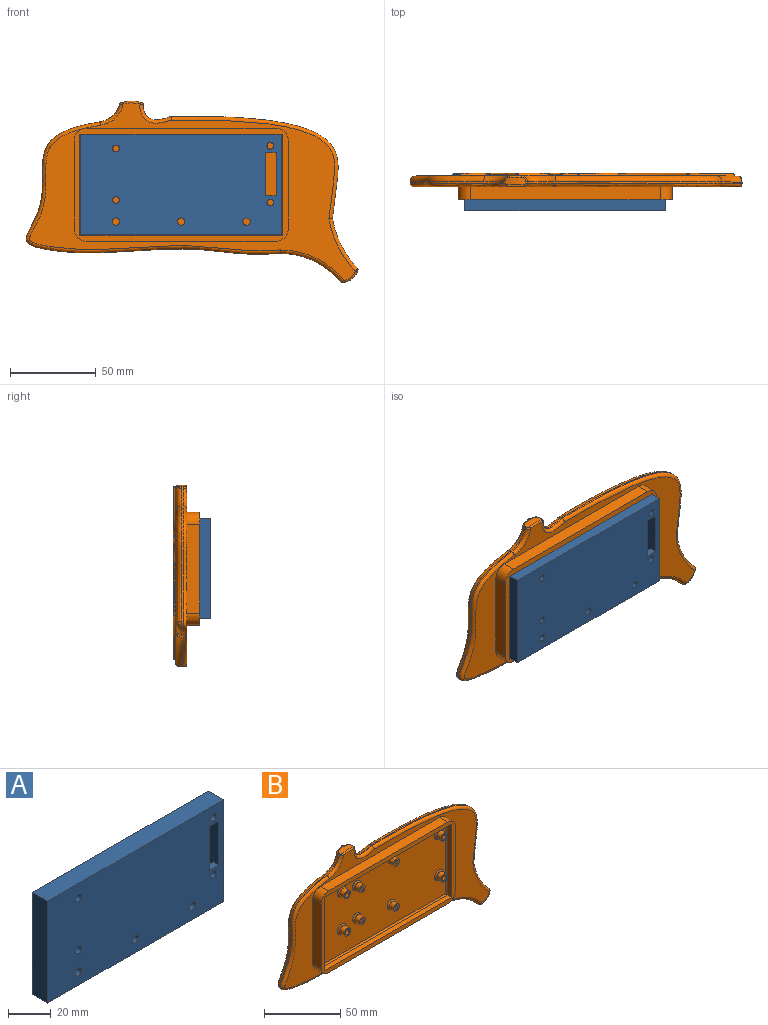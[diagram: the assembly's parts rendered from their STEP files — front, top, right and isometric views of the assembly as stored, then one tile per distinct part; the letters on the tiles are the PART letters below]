
ASSEMBLY  parts=2 mates=1
PART A: 21 faces, bbox 117x10.2x58.6 mm
  f0: cylinder r=2mm len=4mm, axis (0,-1,0), area 47.9mm2, adj f7,f8
  f1: cylinder r=2mm len=4mm, axis (0,-1,0), area 47.9mm2, adj f7,f8
  f2: cylinder r=2mm len=4mm, axis (0,-1,0), area 47.9mm2, adj f7,f8
  f3: cylinder r=2mm len=4mm, axis (0,-1,0), area 47.9mm2, adj f7,f8
  f4: cylinder r=2.12mm len=10.16mm, axis (0,-1,0), area 135.7mm2, adj f8,f17
  f5: cylinder r=2.12mm len=10.16mm, axis (0,-1,0), area 135.7mm2, adj f8,f17
  f6: cylinder r=2.12mm len=10.16mm, axis (0,-1,0), area 135.7mm2, adj f8,f17
  f7: plane 110.53x42.74mm, normal (0,1,0), area 4512.5mm2, adj f0,f1,f2,f3,f13,f14,f15,f16
  f8: plane 117x58.61mm, normal (0,-1,0), area 6603.3mm2, adj f0,f1,f2,f3,f4,f5,f6,f9
  f9: plane 58.61x10.16mm, normal (1,0,0), area 595.5mm2, adj f8,f10,f12,f17
  f10: plane 117x10.16mm, normal (0,0,-1), area 1188.7mm2, adj f8,f9,f11,f17
  f11: plane 58.61x10.16mm, normal (-1,0,0), area 595.5mm2, adj f8,f10,f12,f17
  f12: plane 117x10.16mm, normal (0,0,1), area 1188.7mm2, adj f8,f9,f11,f17
  f13: plane 42.74x10.16mm, normal (-1,0,0), area 368.2mm2, adj f7,f8,f14,f16,f17,f18,f20
  f14: plane 6.35x3.81mm, normal (0,0,1), area 24.2mm2, adj f7,f8,f13,f15
  f15: plane 25.4x3.81mm, normal (1,0,0), area 96.8mm2, adj f7,f8,f14,f16
  f16: plane 6.35x3.81mm, normal (0,0,-1), area 24.2mm2, adj f7,f8,f13,f15
  f17: plane 117x58.61mm, normal (0,1,0), area 2090.8mm2, adj f4,f5,f6,f9,f10,f11,f12,f13
  f18: plane 110.53x6.35mm, normal (0,0,1), area 701.9mm2, adj f7,f13,f17,f19
  f19: plane 42.74x6.35mm, normal (1,0,0), area 271.4mm2, adj f7,f17,f18,f20
  f20: plane 110.53x6.35mm, normal (0,0,-1), area 701.9mm2, adj f7,f13,f17,f19
PART B: 153 faces, bbox 196.2x17.7x108.7 mm
  f0: cylinder r=1mm len=0.93mm, axis (0,-1,0), area 0.9mm2, adj f56,f57,f121,f123
  f1: torus R=4mm, axis (0,-1,0), area 33.2mm2, adj f22,f34
  f2: torus R=3.75mm, axis (0,-1,0), area 30.7mm2, adj f16,f34
  f3: torus R=3.75mm, axis (0,-1,0), area 30.7mm2, adj f18,f34
  f4: torus R=4mm, axis (0,-1,0), area 33.2mm2, adj f20,f34
  f5: torus R=3.75mm, axis (0,-1,0), area 30.7mm2, adj f12,f34
  f6: torus R=4mm, axis (0,-1,0), area 33.2mm2, adj f8,f34
  f7: torus R=4mm, axis (0,-1,0), area 33.2mm2, adj f10,f34
  f8: cylinder r=3mm len=6mm, axis (0,-1,0), area 76.9mm2, adj f6,f49
  f9: cylinder r=1.88mm len=5.08mm, axis (0,-1,0), area 59.8mm2, adj f49,f50
  f10: cylinder r=3mm len=6mm, axis (0,-1,0), area 76.9mm2, adj f7,f47
  f11: cylinder r=1.88mm len=5.08mm, axis (0,-1,0), area 59.8mm2, adj f47,f48
  f12: cylinder r=2.75mm len=5.5mm, axis (0,-1,0), area 70.5mm2, adj f5,f45
  f13: cylinder r=1.2mm len=5.08mm, axis (0,-1,0), area 38.3mm2, adj f45,f46
  f14: cylinder r=2.75mm len=5.5mm, axis (0,-1,0), area 87.8mm2, adj f34,f43
  f15: cylinder r=1.2mm len=5.08mm, axis (0,-1,0), area 38.3mm2, adj f43,f44
  f16: cylinder r=2.75mm len=5.5mm, axis (0,-1,0), area 70.5mm2, adj f2,f41
  f17: cylinder r=1.2mm len=5.08mm, axis (0,-1,0), area 38.3mm2, adj f41,f42
  f18: cylinder r=2.75mm len=5.5mm, axis (0,-1,0), area 70.5mm2, adj f3,f39
  f19: cylinder r=1.2mm len=5.08mm, axis (0,-1,0), area 38.3mm2, adj f39,f40
  f20: cylinder r=3mm len=6mm, axis (0,-1,0), area 76.9mm2, adj f4,f37
  f21: cylinder r=1.88mm len=5.08mm, axis (0,-1,0), area 59.8mm2, adj f37,f38
  f22: cylinder r=3mm len=6mm, axis (0,-1,0), area 76.9mm2, adj f1,f35
  f23: cylinder r=1.88mm len=5.08mm, axis (0,-1,0), area 59.8mm2, adj f35,f36
  f24: plane 189.97x105.24mm, normal (0,1,0), area 10299.5mm2, adj f65,f66,f67,f69,f70,f71,f72,f73
  f25: plane 110.74x7.62mm, normal (0,0,1), area 843.8mm2, adj f33,f55,f82,f84
  f26: plane 51.74x7.62mm, normal (1,0,0), area 394.3mm2, adj f33,f55,f81,f82
  f27: plane 110.74x7.62mm, normal (0,0,-1), area 843.8mm2, adj f33,f55,f81,f83
  f28: plane 59x4.08mm, normal (-1,0,0), area 240.7mm2, adj f29,f31,f33,f53
  f29: plane 118x4.08mm, normal (0,0,-1), area 481.4mm2, adj f28,f30,f33,f51
  f30: plane 59x4.08mm, normal (1,0,0), area 240.7mm2, adj f29,f31,f33,f52
  f31: plane 118x4.08mm, normal (0,0,1), area 481.4mm2, adj f28,f30,f33,f54
  f32: plane 51.74x7.62mm, normal (-1,0,0), area 394.3mm2, adj f33,f55,f83,f84
  f33: plane 124.74x65.74mm, normal (0,-1,0), area 1196.3mm2, adj f25,f26,f27,f28,f29,f30,f31,f32
  f34: plane 116x57mm, normal (0,-1,0), area 6254.6mm2, adj f1,f2,f3,f4,f5,f6,f7,f14
  f35: plane 6x6mm, normal (0,-1,0), area 17.2mm2, adj f22,f23
  f36: plane 3.75x3.75mm, normal (0,-1,0), area 11mm2, adj f23
  f37: plane 6x6mm, normal (0,-1,0), area 17.2mm2, adj f20,f21
  f38: plane 3.75x3.75mm, normal (0,-1,0), area 11mm2, adj f21
  f39: plane 5.5x5.5mm, normal (0,-1,0), area 19.2mm2, adj f18,f19
  f40: plane 2.4x2.4mm, normal (0,-1,0), area 4.5mm2, adj f19
  f41: plane 5.5x5.5mm, normal (0,-1,0), area 19.2mm2, adj f16,f17
  f42: plane 2.4x2.4mm, normal (0,-1,0), area 4.5mm2, adj f17
  f43: plane 5.5x5.5mm, normal (0,-1,0), area 19.2mm2, adj f14,f15
  f44: plane 2.4x2.4mm, normal (0,-1,0), area 4.5mm2, adj f15
  f45: plane 5.5x5.5mm, normal (0,-1,0), area 19.2mm2, adj f12,f13
  f46: plane 2.4x2.4mm, normal (0,-1,0), area 4.5mm2, adj f13
  f47: plane 6x6mm, normal (0,-1,0), area 17.2mm2, adj f10,f11
  f48: plane 3.75x3.75mm, normal (0,-1,0), area 11mm2, adj f11
  f49: plane 6x6mm, normal (0,-1,0), area 17.2mm2, adj f8,f9
  f50: plane 3.75x3.75mm, normal (0,-1,0), area 11mm2, adj f9
  f51: cylinder r=1mm len=118mm, axis (-1,0,0), area 183.8mm2, adj f29,f34,f52,f53
  f52: cylinder r=1mm len=59mm, axis (0,0,-1), area 91.1mm2, adj f30,f34,f51,f54
  f53: cylinder r=1mm len=59mm, axis (0,0,1), area 91.1mm2, adj f28,f34,f51,f54
  f54: cylinder r=1mm len=118mm, axis (1,0,0), area 183.8mm2, adj f31,f34,f52,f53
  f55: plane 190.91x104.44mm, normal (0,-1,0), area 4269.5mm2, adj f25,f26,f27,f32,f74,f75,f76,f77
  f56: extruded ~8.84x7.31mm, area 48.1mm2, adj f0,f121,f122,f123,f124,f125,f126,f127
  f57: extruded ~35.27x16.8mm, area 34.3mm2, adj f0,f58,f65,f80
  f58: extruded ~134.16x3.26mm, area 114.3mm2, adj f57,f59,f66,f79
  f59: extruded ~74.67x43.04mm, area 91.8mm2, adj f58,f60,f67,f68,f69,f78
  f60: extruded ~11.58x10.44mm, area 14mm2, adj f59,f70,f77,f133
  f61: extruded ~12.3x4.35mm, area 50.1mm2, adj f128,f129,f130,f131,f132,f133,f134,f135
  f62: extruded ~16.25x8.94mm, area 19mm2, adj f63,f73,f74,f130
  f63: extruded ~97.36x59.72mm, area 120mm2, adj f62,f64,f72,f75
  f64: extruded ~28.97x14.63mm, area 28mm2, adj f63,f71,f76,f126
  f65: bspline ~39.31x21.41mm, area 231.2mm2, adj f24,f57,f66,f123
  f66: bspline ~135.26x6.83mm, area 738.2mm2, adj f24,f58,f65,f67
  f67: bspline ~13.97x6.75mm, area 72.9mm2, adj f24,f59,f66,f68
  f68: bspline ~3.52x3.5mm, area 7.1mm2, adj f59,f67,f69
  f69: bspline ~68.1x44.19mm, area 490.3mm2, adj f24,f59,f68,f70
  f70: bspline ~15.55x15.32mm, area 102.2mm2, adj f24,f60,f69,f131
  f71: bspline ~32.97x19.02mm, area 189mm2, adj f24,f64,f72,f127
  f72: bspline ~98.2x61.07mm, area 764mm2, adj f24,f63,f71,f73
  f73: bspline ~21.21x13.27mm, area 136mm2, adj f24,f62,f72,f128
  f74: bspline ~19.13x11.43mm, area 74.3mm2, adj f55,f62,f75,f132
  f75: bspline ~98.21x60.86mm, area 439.4mm2, adj f55,f63,f74,f76
  f76: bspline ~31.34x17.15mm, area 105.9mm2, adj f55,f64,f75,f124
  f77: bspline ~13.85x13.1mm, area 55.3mm2, adj f55,f60,f78,f135
  f78: bspline ~74.85x44.02mm, area 333.3mm2, adj f55,f59,f77,f79
  f79: bspline ~135.87x5.3mm, area 422.1mm2, adj f55,f58,f78,f80
  f80: bspline ~37.67x19.43mm, area 129.7mm2, adj f55,f57,f79,f121
  f81: cylinder r=7mm len=7.62mm, axis (0,1,0), area 83.8mm2, adj f26,f27,f33,f55
  f82: cylinder r=7mm len=7.62mm, axis (0,-1,0), area 83.8mm2, adj f25,f26,f33,f55
  f83: cylinder r=7mm len=7.62mm, axis (0,-1,0), area 83.8mm2, adj f27,f32,f33,f55
  f84: cylinder r=7mm len=7.62mm, axis (0,1,0), area 83.8mm2, adj f25,f32,f33,f55
  f85: plane 8.4x4.1mm, normal (-0.91,0,0.42), area 4.8mm2, adj f24,f101,f102,f118,f119
  f86: plane 40.05x10.78mm, normal (0,1,0), area 22.3mm2, adj f101,f102,f103
  f87: plane 3x0.99mm, normal (0.99,0,-0.1), area 2.3mm2, adj f24,f151,f152
  f88: plane 75.01x27.17mm, normal (0,1,0), area 97.2mm2, adj f104,f105,f106
  f89: plane 1.35x0.99mm, normal (-0.59,0,0.81), area 1.1mm2, adj f24,f144,f145
  f90: plane 2.91x2.23mm, normal (0.59,0,-0.81), area 2mm2, adj f24,f114,f146
  f91: plane 4.75x3.81mm, normal (0,1,0), area 0.8mm2, adj f114,f115
  f92: plane 1.22x1mm, normal (0.63,0,-0.77), area 0.9mm2, adj f24,f140,f141
  f93: plane 1.44x1.18mm, normal (-0.63,0,0.77), area 1.2mm2, adj f24,f142,f143
  f94: plane 5.91x5.25mm, normal (0,1,0), area 1.8mm2, adj f112,f113
  f95: plane 1.08x0.91mm, normal (-0.53,0,0.85), area 0.8mm2, adj f24,f149,f150
  f96: plane 1.06x0.95mm, normal (0.76,0,-0.65), area 1mm2, adj f24,f138,f139
  f97: plane 39.71x31.6mm, normal (0,1,0), area 132.9mm2, adj f107,f108,f109,f110,f111
  f98: plane 0.7x0.51mm, normal (0.77,0,-0.64), area 0.3mm2, adj f24,f147,f148
  f99: plane 1.01x0.9mm, normal (0,0,1), area 0.6mm2, adj f129,f136,f137
  f100: plane 22.1x17.45mm, normal (0,1,0), area 63.8mm2, adj f116,f117
  f101: bspline ~64.26x28.66mm, area 85.5mm2, adj f85,f86,f102,f103,f118
  f102: bspline ~63.83x27.77mm, area 84.2mm2, adj f85,f86,f101,f103,f119
  f103: cylinder r=1mm len=3.35mm, axis (-0.42,0,-0.91), area 2.8mm2, adj f86,f101,f102,f120
  f104: bspline ~84x35.03mm, area 215.4mm2, adj f24,f88,f105,f106,f151,f152
  f105: bspline ~83.52x33.4mm, area 211.2mm2, adj f24,f88,f104,f106,f151
  f106: cylinder r=1.5mm len=4.91mm, axis (-0.1,0,-0.99), area 7.7mm2, adj f24,f88,f104,f105
  f107: bspline ~26.94x6.1mm, area 59.9mm2, adj f24,f97,f108,f109
  f108: cylinder r=1.5mm len=4.13mm, axis (-0.62,0,-0.79), area 6.2mm2, adj f24,f97,f107,f110
  f109: bspline ~24.52x3.75mm, area 52.3mm2, adj f24,f97,f107,f111,f149,f150
  f110: bspline ~53.31x27.32mm, area 136mm2, adj f24,f97,f108,f111,f138
  f111: bspline ~46.99x27.97mm, area 118.9mm2, adj f24,f97,f109,f110,f138,f139,f149
  f112: bspline ~16.59x16.42mm, area 57.2mm2, adj f24,f94,f113,f140,f141,f142,f143
  f113: bspline ~16.21x15.98mm, area 52.2mm2, adj f24,f94,f112,f140,f142
  f114: bspline ~25.08x23.59mm, area 78.4mm2, adj f24,f90,f91,f115,f144,f146
  f115: bspline ~24.07x23.57mm, area 80.3mm2, adj f24,f91,f114,f144,f145,f146
  f116: bspline ~31.78x22.39mm, area 94.9mm2, adj f24,f100,f117,f136,f147
  f117: bspline ~31.62x25.4mm, area 112.7mm2, adj f24,f100,f116,f136,f137,f147,f148
  f118: bspline ~64.74x27.62mm, area 91.5mm2, adj f24,f85,f101,f120
  f119: bspline ~65.72x29.49mm, area 93.5mm2, adj f24,f85,f102,f120
  f120: cylinder r=1mm len=5.32mm, axis (-0.42,0,-0.91), area 5.7mm2, adj f24,f103,f118,f119
  f121: bspline ~2.12x2mm, area 3.2mm2, adj f0,f56,f80,f122
  f122: bspline ~7.45x6.4mm, area 14.7mm2, adj f55,f56,f121,f124
  f123: bspline ~3.78x3.5mm, area 6.5mm2, adj f0,f56,f65,f125
  f124: bspline ~2.12x2mm, area 3.3mm2, adj f56,f76,f122,f126
  f125: bspline ~5.09x4.47mm, area 9.4mm2, adj f24,f56,f123,f127
  f126: cylinder r=1mm len=1.04mm, axis (0,-1,0), area 0.9mm2, adj f56,f64,f124,f127
  f127: bspline ~3.61x3.5mm, area 6.7mm2, adj f56,f71,f125,f126
  f128: bspline ~3.5x3.49mm, area 7mm2, adj f61,f73,f129,f130
  f129: bspline ~6.79x1.3mm, area 10.1mm2, adj f24,f61,f99,f128,f131,f136,f137
  f130: cylinder r=1mm len=0.95mm, axis (0,-1,0), area 1.1mm2, adj f61,f62,f128,f132
  f131: bspline ~3.73x3.5mm, area 6.3mm2, adj f61,f70,f129,f133
  f132: bspline ~2x2mm, area 3.5mm2, adj f61,f74,f130,f134
  f133: cylinder r=1mm len=0.85mm, axis (0,-1,0), area 0.8mm2, adj f60,f61,f131,f135
  f134: bspline ~10.08x1.63mm, area 15.7mm2, adj f55,f61,f132,f135
  f135: bspline ~2.09x2mm, area 3.1mm2, adj f61,f77,f133,f134
  f136: bspline ~1.57x1.5mm, area 1.5mm2, adj f24,f99,f116,f117,f129,f137
  f137: bspline ~1.42x1.12mm, area 0.8mm2, adj f24,f99,f117,f129,f136
  f138: bspline ~1.49x1.37mm, area 1.6mm2, adj f24,f96,f110,f111,f139
  f139: bspline ~1.47x1.27mm, area 1.3mm2, adj f24,f96,f111,f138
  f140: bspline ~1.62x1.42mm, area 2mm2, adj f24,f92,f112,f113,f141
  f141: bspline ~1.32x1mm, area 0.6mm2, adj f24,f92,f112,f140
  f142: bspline ~2.15x1.59mm, area 2.1mm2, adj f24,f93,f112,f113,f143
  f143: bspline ~1.43x1.15mm, area 0.8mm2, adj f24,f93,f112,f142
  f144: bspline ~1.53x1.44mm, area 2.1mm2, adj f24,f89,f114,f115,f145
  f145: bspline ~1.39x1.11mm, area 0.8mm2, adj f24,f89,f115,f144
  f146: bspline ~1.88x1.33mm, area 0.6mm2, adj f24,f90,f114,f115
  f147: bspline ~1.44x1.26mm, area 1.3mm2, adj f24,f98,f116,f117,f148
  f148: bspline ~1.25x0.76mm, area 0.6mm2, adj f24,f98,f117,f147
  f149: bspline ~1.48x1.39mm, area 1.5mm2, adj f24,f95,f109,f111,f150
  f150: bspline ~1.43x1.05mm, area 0.9mm2, adj f24,f95,f109,f149
  f151: bspline ~3.16x1.6mm, area 2.7mm2, adj f24,f87,f104,f105,f152
  f152: bspline ~1.85x1.49mm, area 1.1mm2, adj f24,f87,f104,f151
PLACE A t=(0,-28.19,0)mm
PLACE B t=(0,-21.84,-0.19)mm
MATE slider B.f7 <-> A.f3  axis (0,-1,0) through (52,-21.84,-10.57)mm
